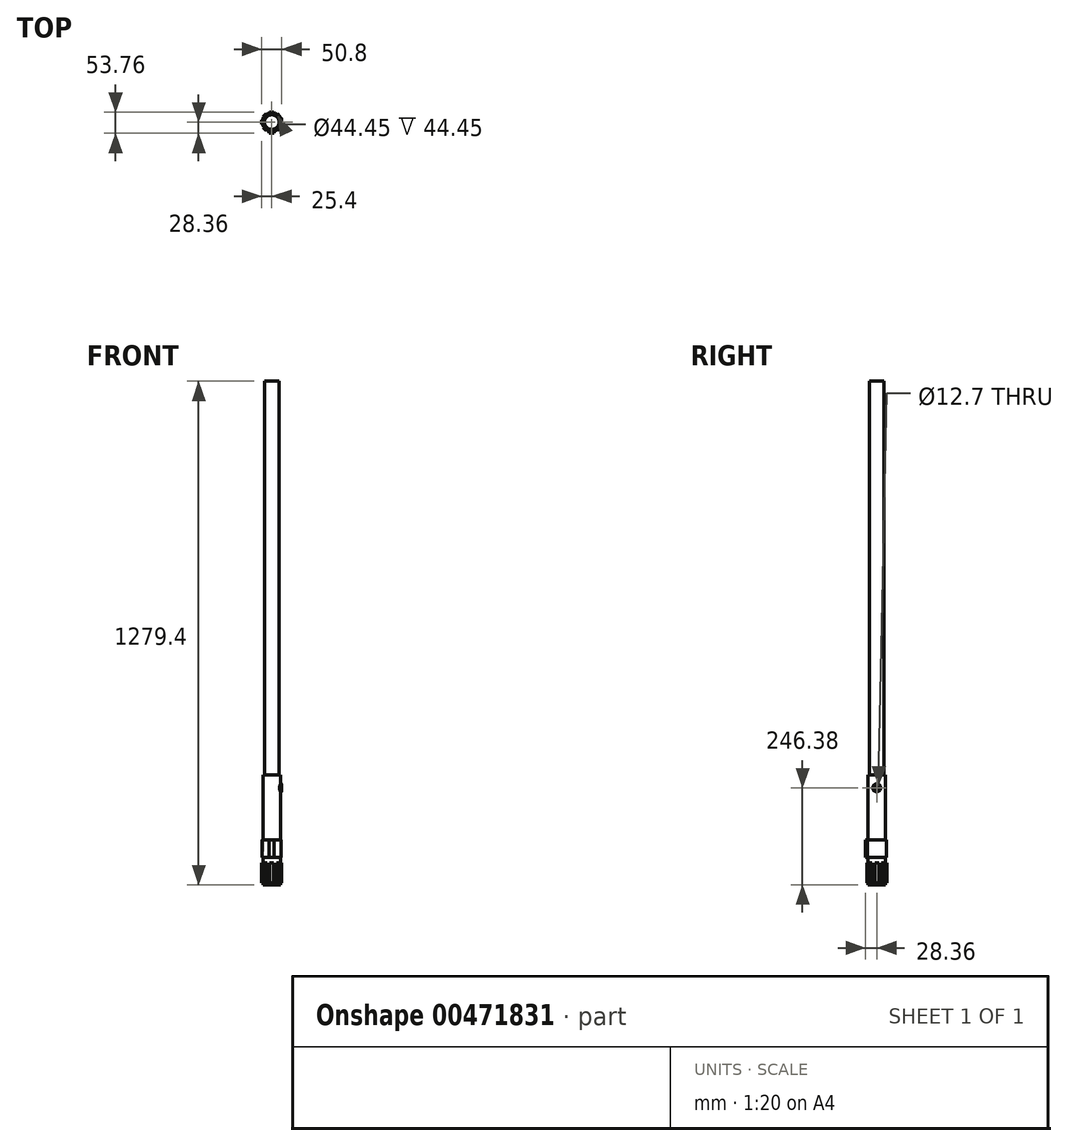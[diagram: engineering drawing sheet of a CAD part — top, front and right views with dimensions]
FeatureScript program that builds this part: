
annotation { "Feature Type Name" : "Feature", "Feature Type Description" : "" }
export const myFeature = defineFeature(function(context is Context, id is Id, definition is map)
    precondition{}
    {
        {
            var Q0;
            Q0=qCreatedBy(makeId("Right.planeOp"),FACE);
            cPlane(context, id + "F0", {"entities" : qUnion([Q0]), "cplaneType" : CPlaneType.OFFSET, "offset" : 25.4 * mm, "width" : 152.4 * mm, "height" : 152.4 * mm});
        }
        {
            var Q0;
            Q0=qCreatedBy(makeId("Top.planeOp"),FACE);
            var sketch = newSketch(context, id + "F1", { "sketchPlane" : qUnion([Q0])});
            skCircle(sketch, "E0", {"center": v(0, 0) * mm, "radius": 22.23 * mm});
            skSolve(sketch);
        }
        {
            var Q0;
            Q0 = qSketchRegion(id + "F1", true);
            extrude(context, id + "F2", {"entities" : qUnion([Q0]), "endBound" : BoundingType.SYMMETRIC, "depth" : 279.4 * mm});
        }
        {
            var Q0;
            Q0=qCreatedBy(id+"F0.planeOp",FACE);
            var sketch = newSketch(context, id + "F3", { "sketchPlane" : qUnion([Q0])});
            skLineSegment(sketch, "E1.bottom", {"start": v(5.08, -134.62) * mm, "end": v(-5.08, -134.62) * mm});
            skLineSegment(sketch, "E1.top", {"start": v(5.08, -83.82) * mm, "end": v(-5.08, -83.82) * mm});
            skLineSegment(sketch, "E1.left", {"start": v(5.08, -134.62) * mm, "end": v(5.08, -83.82) * mm});
            skLineSegment(sketch, "E1.right", {"start": v(-5.08, -134.62) * mm, "end": v(-5.08, -83.82) * mm});
            skSolve(sketch);
        }
        {
            var Q0;
            Q0=makeQuery(id+"F3.imprint","IMPRINT",FACE,{"disambiguationData":[TD([[makeQuery(id+"F3.imprint","IMPRINT",EDGE,{"derivedFrom":sQuery(id+"F3.wireOp",EDGE,"E1.bottom")}),-1.0]])]});
            var Q1;
            Q1=makeQuery(id+"F2.opExtrude","SWEPT_FACE",FACE,{"disambiguationData":[OSD([sQuery(id+"F1.wireOp",EDGE,"E0")])]});
            extrude(context, id + "F4", {"entities" : qUnion([Q0]), "endBound" : BoundingType.UP_TO_SURFACE, "oppositeDirection" : true, "endBoundEntityFace" : qUnion([Q1]), "depth" : 25.4 * mm});
        }
        {
            var Q0;
            Q0=qCreatedBy(makeId("Right.planeOp"),FACE);
            var sketch = newSketch(context, id + "F5", { "sketchPlane" : qUnion([Q0])});
            skLineSegment(sketch, "E2", {"start": v(0, 31.7) * mm, "end": v(0, 0) * mm});
            skSolve(sketch);
        }
        {
            var Q0;
            Q0=makeQuery(id+"F4.opExtrude","SWEPT_BODY",BODY,{"disambiguationData":[OSD([sQuery(id+"F3.wireOp",EDGE,"E1.bottom"),sQuery(id+"F3.wireOp",EDGE,"E1.top"),sQuery(id+"F3.wireOp",EDGE,"E1.left"),sQuery(id+"F3.wireOp",EDGE,"E1.right")])]});
            var Q1;
            Q1=sQuery(id+"F5.wireOp",EDGE,"E2");
            circularPattern(context, id + "F6", {"entities" : qUnion([Q0]), "axis" : qUnion([Q1]), "angle" : 360 * degree, "instanceCount" : 8, "equalSpace" : true});
        }
        {
            var Q0;
            Q0=qCreatedBy(makeId("Top.planeOp"),FACE);
            cPlane(context, id + "F7", {"entities" : qUnion([Q0]), "cplaneType" : CPlaneType.OFFSET, "offset" : 25.4 * mm, "oppositeDirection" : true, "width" : 152.4 * mm, "height" : 152.4 * mm});
        }
        {
            var Q0;
            Q0=qCreatedBy(id+"F7.planeOp",FACE);
            var sketch = newSketch(context, id + "F8", { "sketchPlane" : qUnion([Q0])});
            skCircle(sketch, "E3", {"center": v(0, 0) * mm, "radius": 22.23 * mm});
            skArc(sketch, "E4", {"start": v(6.35, -23.28) * mm, "mid": v(0, 24.13) * mm, "end": v(-6.35, -23.28) * mm});
            skLineSegment(sketch, "E5.top", {"start": v(-6.35, -28.36) * mm, "end": v(6.35, -28.36) * mm});
            skLineSegment(sketch, "E5.left", {"start": v(-6.35, -23.28) * mm, "end": v(-6.35, -28.36) * mm});
            skLineSegment(sketch, "E5.right", {"start": v(6.35, -23.28) * mm, "end": v(6.35, -28.36) * mm});
            skSolve(sketch);
        }
        {
            var Q0;
            Q0 = qSketchRegion(id + "F8", true);
            extrude(context, id + "F9", {"entities" : qUnion([Q0]), "oppositeDirection" : true, "depth" : 44.45 * mm});
        }
        {
            var Q0;
            Q0=qCreatedBy(id+"F0.planeOp",FACE);
            var sketch = newSketch(context, id + "F10", { "sketchPlane" : qUnion([Q0])});
            skCircle(sketch, "E6", {"center": v(0, 106.68) * mm, "radius": 6.35 * mm});
            skCircle(sketch, "E7", {"center": v(0, 106.68) * mm, "radius": 10.16 * mm});
            skSolve(sketch);
        }
        {
            var Q0;
            Q0 = qSketchRegion(id + "F10", true);
            var Q1;
            Q1=makeQuery(id+"F2.opExtrude","SWEPT_FACE",FACE,{"disambiguationData":[OSD([sQuery(id+"F1.wireOp",EDGE,"E0")])]});
            extrude(context, id + "F11", {"entities" : qUnion([Q0]), "endBound" : BoundingType.UP_TO_SURFACE, "oppositeDirection" : true, "endBoundEntityFace" : qUnion([Q1]), "depth" : 25.4 * mm});
        }
        {
            var Q0;
            Q0=makeQuery(id+"F11.opExtrude","CAP_EDGE",EDGE,{"disambiguationData":[OSD([sQuery(id+"F10.wireOp",EDGE,"E6")])],"isStart":true});
            chamfer(context, id + "F12", {"entities" : qUnion([Q0]), "width" : 2.54 * mm, "tangentPropagation" : true});
        }
        {
            var Q0;
            Q0=makeQuery(id+"F12.opChamfer","BLEND_FACE",FACE,{"disambiguationData":[OSD([sQuery(id+"F10.wireOp",EDGE,"E6")])]});
            var Q1;
            Q1=makeQuery(id+"F11.opExtrude","CAP_EDGE",EDGE,{"disambiguationData":[OSD([sQuery(id+"F10.wireOp",EDGE,"E7")])],"isStart":true});
            fillet(context, id + "F13", {"entities" : qUnion([Q0, Q1]), "radius" : 0.76 * mm, "tangentPropagation" : true, "allowEdgeOverflow" : false});
        }
        {
            var Q0;
            Q0=qCreatedBy(id+"F0.planeOp",FACE);
            var sketch = newSketch(context, id + "F14", { "sketchPlane" : qUnion([Q0])});
            skCircle(sketch, "E8", {"center": v(0, 106.68) * mm, "radius": 5.72 * mm});
            skSolve(sketch);
        }
        {
            var Q0;
            Q0 = qSketchRegion(id + "F14", true);
            var Q1;
            Q1=makeQuery(id+"F2.opExtrude","SWEPT_FACE",FACE,{"disambiguationData":[OSD([sQuery(id+"F1.wireOp",EDGE,"E0")])]});
            extrude(context, id + "F15", {"entities" : qUnion([Q0]), "endBound" : BoundingType.UP_TO_SURFACE, "oppositeDirection" : true, "endBoundEntityFace" : qUnion([Q1]), "depth" : 25.4 * mm});
        }
        {
            var Q0;
            Q0=makeQuery(id+"F15.opExtrude","CAP_FACE",FACE,{"disambiguationData":[OSD([sQuery(id+"F14.wireOp",EDGE,"E8")])],"isStart":true});
            fillet(context, id + "F16", {"entities" : qUnion([Q0]), "radius" : 2.54 * mm, "tangentPropagation" : true, "allowEdgeOverflow" : false});
        }
        {
            var Q0;
            Q0=makeQuery(id+"F2.opExtrude","CAP_FACE",FACE,{"disambiguationData":[OSD([sQuery(id+"F1.wireOp",EDGE,"E0")])],"isStart":false});
            var sketch = newSketch(context, id + "F17", { "sketchPlane" : qUnion([Q0])});
            skCircle(sketch, "E9", {"center": v(0, 0) * mm, "radius": 18.67 * mm});
            skSolve(sketch);
        }
        {
            var Q0;
            Q0 = qSketchRegion(id + "F17", true);
            extrude(context, id + "F18", {"entities" : qUnion([Q0]), "depth" : 1000 * mm});
        }
    });
